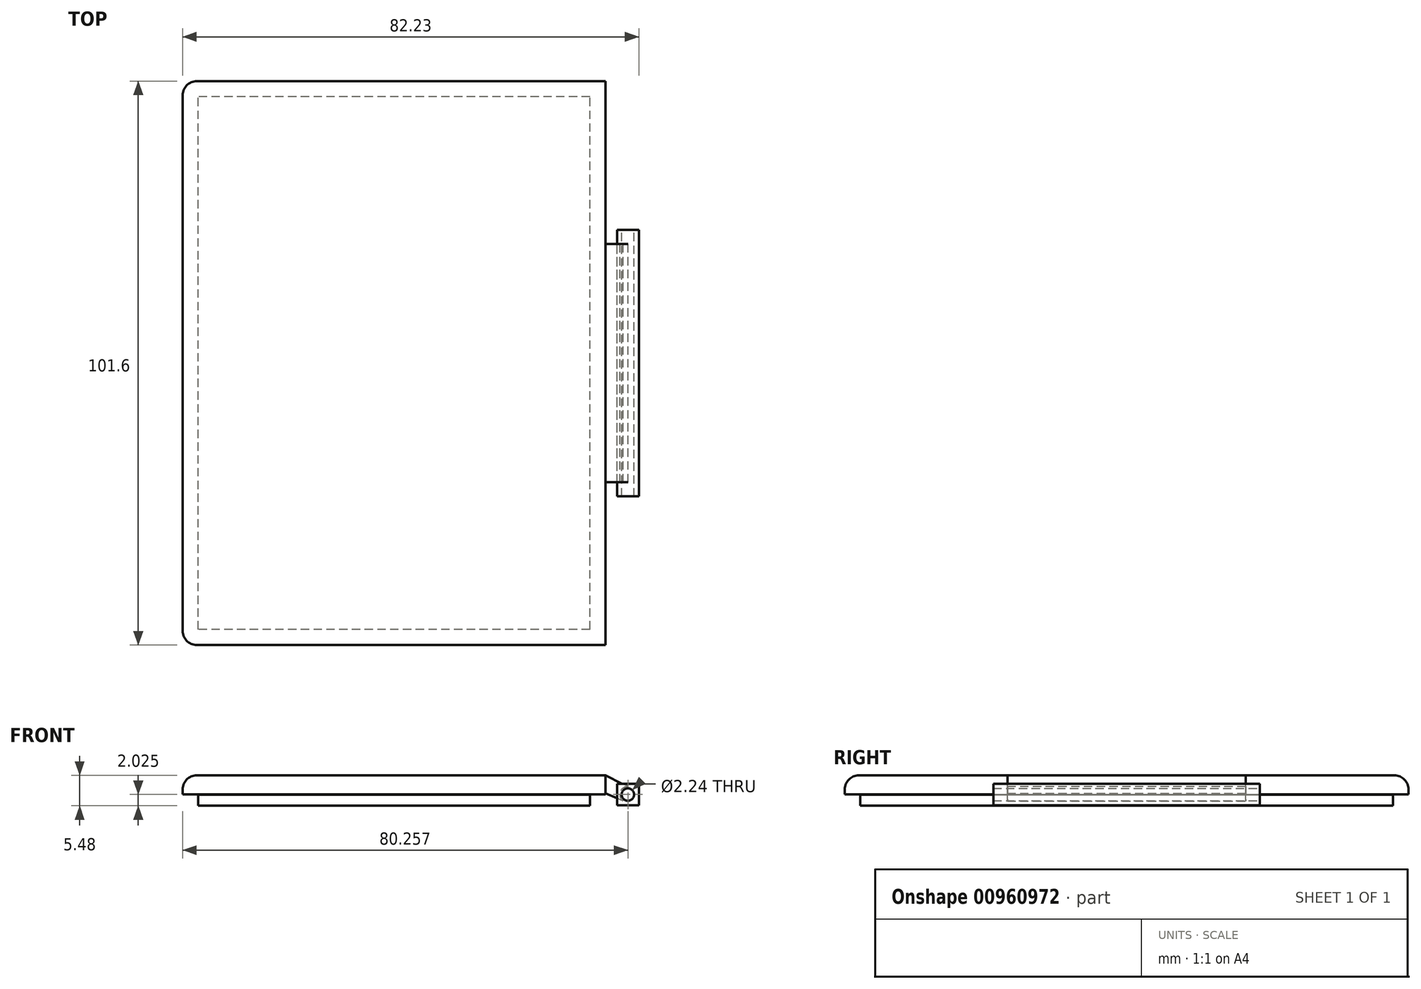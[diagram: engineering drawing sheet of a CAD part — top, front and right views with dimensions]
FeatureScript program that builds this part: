
annotation { "Feature Type Name" : "Feature", "Feature Type Description" : "" }
export const myFeature = defineFeature(function(context is Context, id is Id, definition is map)
    precondition{}
    {
        {
            var Q0;
            Q0=qCreatedBy(makeId("Front.planeOp"),FACE);
            var sketch = newSketch(context, id + "F0", { "sketchPlane" : qUnion([Q0])});
            skPoint(sketch, "E0", {"position": v(0, 1.2) * mm});
            skLineSegment(sketch, "E1.bottom", {"start": v(38.1, -0.54) * mm, "end": v(-38.1, -0.54) * mm});
            skLineSegment(sketch, "E1.top", {"start": v(38.1, 2.92) * mm, "end": v(-38.1, 2.92) * mm});
            skLineSegment(sketch, "E1.left", {"start": v(38.1, -0.54) * mm, "end": v(38.1, 2.92) * mm});
            skLineSegment(sketch, "E1.right", {"start": v(-38.1, -0.54) * mm, "end": v(-38.1, 2.92) * mm});
            skPoint(sketch, "E2", {"position": v(0, -1.55) * mm});
            skLineSegment(sketch, "E3.bottom", {"start": v(35.3, -2.56) * mm, "end": v(-35.3, -2.56) * mm});
            skLineSegment(sketch, "E3.top", {"start": v(35.3, -0.54) * mm, "end": v(-35.3, -0.54) * mm});
            skLineSegment(sketch, "E3.left", {"start": v(35.3, -2.56) * mm, "end": v(35.3, -0.54) * mm});
            skLineSegment(sketch, "E3.right", {"start": v(-35.3, -2.56) * mm, "end": v(-35.3, -0.54) * mm});
            skCircle(sketch, "E4", {"center": v(42.16, -0.54) * mm, "radius": 1.46 * mm});
            skPoint(sketch, "E4.centerSnap0", {"position": v(0, -0.54) * mm});
            skLineSegment(sketch, "E5", {"start": v(41.3, -1.71) * mm, "end": v(38.1, -0.3) * mm});
            skCircle(sketch, "E6", {"center": v(42.16, -0.54) * mm, "radius": 1.12 * mm});
            skLineSegment(sketch, "E7", {"start": v(42.16, 0.93) * mm, "end": v(38.1, 2.92) * mm});
            skLineSegment(sketch, "E8.bottom", {"start": v(44.13, -2.5) * mm, "end": v(40.19, -2.5) * mm});
            skLineSegment(sketch, "E8.top", {"start": v(44.13, 1.43) * mm, "end": v(40.19, 1.43) * mm});
            skLineSegment(sketch, "E8.left", {"start": v(44.13, -2.5) * mm, "end": v(44.13, 1.43) * mm});
            skLineSegment(sketch, "E8.right", {"start": v(40.19, -2.5) * mm, "end": v(40.19, 1.43) * mm});
            skSolve(sketch);
        }
        {
            var Q0;
            Q0=makeQuery(id+"F0.imprint","IMPRINT",FACE,{"disambiguationData":[TD([[makeQuery(id+"F0.imprint","IMPRINT",EDGE,{"derivedFrom":sQuery(id+"F0.wireOp",EDGE,"E1.top")}),1.0]])]});
            var Q1;
            {var subQ0=sQuery(id+"F0.wireOp",EDGE,"E1.right");Q1=makeQuery(id+"F0.imprint","IMPRINT",FACE,{"disambiguationData":[TD([[makeQuery(id+"F0.imprint","IMPRINT",EDGE,{"derivedFrom":subQ0}),-1.0]])]});}
            extrude(context, id + "F1", {"entities" : qUnion([Q0, Q1]), "endBound" : BoundingType.SYMMETRIC, "depth" : 101.6 * mm, "offsetDistance" : 25.4 * mm});
        }
        {
            var Q0;
            {var subQ5=sQuery(id+"F0.wireOp",EDGE,"E3.bottom");Q0=makeQuery(id+"F0.imprint","IMPRINT",FACE,{"disambiguationData":[TD([[makeQuery(id+"F0.imprint","IMPRINT",EDGE,{"derivedFrom":subQ5}),-1.0]])]});}
            extrude(context, id + "F2", {"entities" : qUnion([Q0]), "endBound" : BoundingType.SYMMETRIC, "depth" : 96.01 * mm, "offsetDistance" : 25.4 * mm});
        }
        {
            var Q0;
            Q0=makeQuery(id+"F1.opExtrude","CAP_EDGE",EDGE,{"disambiguationData":[OSD([sQuery(id+"F0.wireOp",EDGE,"E1.top")])],"isStart":true});
            var Q1;
            Q1=makeQuery(id+"F1.opExtrude","SWEPT_EDGE",EDGE,{"disambiguationData":[OSD([sQuery(id+"F0.wireOp",EDGE,"E1.top"),sQuery(id+"F0.wireOp",EDGE,"E1.right")])]});
            var Q2;
            Q2=makeQuery(id+"F1.opExtrude","CAP_EDGE",EDGE,{"disambiguationData":[OSD([sQuery(id+"F0.wireOp",EDGE,"E1.top")])],"isStart":false});
            fillet(context, id + "F3", {"entities" : qUnion([Q0, Q1, Q2]), "radius" : 2.54 * mm, "tangentPropagation" : true, "allowEdgeOverflow" : false});
        }
        {
            var Q0;
            {var subQ0=sQuery(id+"F0.wireOp",EDGE,"E1.top");Q0=makeQuery(id+"F3.opFillet","BLEND_EDGE",EDGE,{"blendedFrom":[makeQuery(id+"F1.opExtrude","SWEPT_EDGE",EDGE,{"disambiguationData":[OSD([subQ0,sQuery(id+"F0.wireOp",EDGE,"E1.left")])]}),makeQuery(id+"F1.opExtrude","CAP_EDGE",EDGE,{"disambiguationData":[OSD([subQ0])],"isStart":true})],"blendedInto":[]});}
            var Q1;
            {var subQ0=sQuery(id+"F0.wireOp",EDGE,"E1.top");Q1=makeQuery(id+"F3.opFillet","BLEND_EDGE",EDGE,{"blendedFrom":[makeQuery(id+"F1.opExtrude","SWEPT_EDGE",EDGE,{"disambiguationData":[OSD([subQ0,sQuery(id+"F0.wireOp",EDGE,"E1.right")])]}),makeQuery(id+"F1.opExtrude","CAP_EDGE",EDGE,{"disambiguationData":[OSD([subQ0])],"isStart":true})],"blendedInto":[]});}
            var Q2;
            {var subQ0=sQuery(id+"F0.wireOp",EDGE,"E1.top");Q2=makeQuery(id+"F3.opFillet","BLEND_EDGE",EDGE,{"blendedFrom":[makeQuery(id+"F1.opExtrude","SWEPT_EDGE",EDGE,{"disambiguationData":[OSD([subQ0,sQuery(id+"F0.wireOp",EDGE,"E1.right")])]}),makeQuery(id+"F1.opExtrude","CAP_EDGE",EDGE,{"disambiguationData":[OSD([subQ0])],"isStart":false})],"blendedInto":[]});}
            var Q3;
            {var subQ0=sQuery(id+"F0.wireOp",EDGE,"E1.top");Q3=makeQuery(id+"F3.opFillet","BLEND_EDGE",EDGE,{"blendedFrom":[makeQuery(id+"F1.opExtrude","SWEPT_EDGE",EDGE,{"disambiguationData":[OSD([subQ0,sQuery(id+"F0.wireOp",EDGE,"E1.left")])]}),makeQuery(id+"F1.opExtrude","CAP_EDGE",EDGE,{"disambiguationData":[OSD([subQ0])],"isStart":false})],"blendedInto":[]});}
            fillet(context, id + "F4", {"entities" : qUnion([Q0, Q1, Q2, Q3]), "radius" : 2.54 * mm, "tangentPropagation" : true, "allowEdgeOverflow" : false});
        }
        {
            var Q0;
            Q0=makeQuery(id+"F0.imprint","IMPRINT",FACE,{"disambiguationData":[TD([[makeQuery(id+"F0.imprint","IMPRINT",EDGE,{"derivedFrom":sQuery(id+"F0.wireOp",EDGE,"E6")}),-1.0]])]});
            var Q1;
            {var subQ5=sQuery(id+"F0.wireOp",EDGE,"E5");var subQ6=sQuery(id+"F0.wireOp",EDGE,"E4");var subQ7=makeQuery(id+"F0.imprint","INTERSECT",VERTEX,{"derivedFrom":[subQ6,subQ5]});Q1=makeQuery(id+"F0.imprint","IMPRINT",FACE,{"disambiguationData":[TD([[makeQuery(id+"F0.imprint","IMPRINT",EDGE,{"disambiguationData":[TD([[subQ7,1.0]])],"derivedFrom":subQ6}),-1.0]])]});}
            var Q2;
            {var subQ5=sQuery(id+"F0.wireOp",EDGE,"E8.bottom");Q2=makeQuery(id+"F0.imprint","IMPRINT",FACE,{"disambiguationData":[TD([[makeQuery(id+"F0.imprint","IMPRINT",EDGE,{"derivedFrom":subQ5}),-1.0]])]});}
            extrude(context, id + "F5", {"entities" : qUnion([Q0, Q1, Q2]), "endBound" : BoundingType.SYMMETRIC, "depth" : 48.06 * mm, "offsetDistance" : 25.4 * mm});
        }
        {
            var Q0;
            {var subQ0=sQuery(id+"F0.wireOp",EDGE,"E5");Q0=makeQuery(id+"F0.imprint","IMPRINT",FACE,{"disambiguationData":[TD([[makeQuery(id+"F0.imprint","IMPRINT",EDGE,{"derivedFrom":subQ0}),-1.0]])]});}
            extrude(context, id + "F6", {"entities" : qUnion([Q0]), "endBound" : BoundingType.SYMMETRIC, "depth" : 42.98 * mm, "offsetDistance" : 25.4 * mm});
        }
    });
